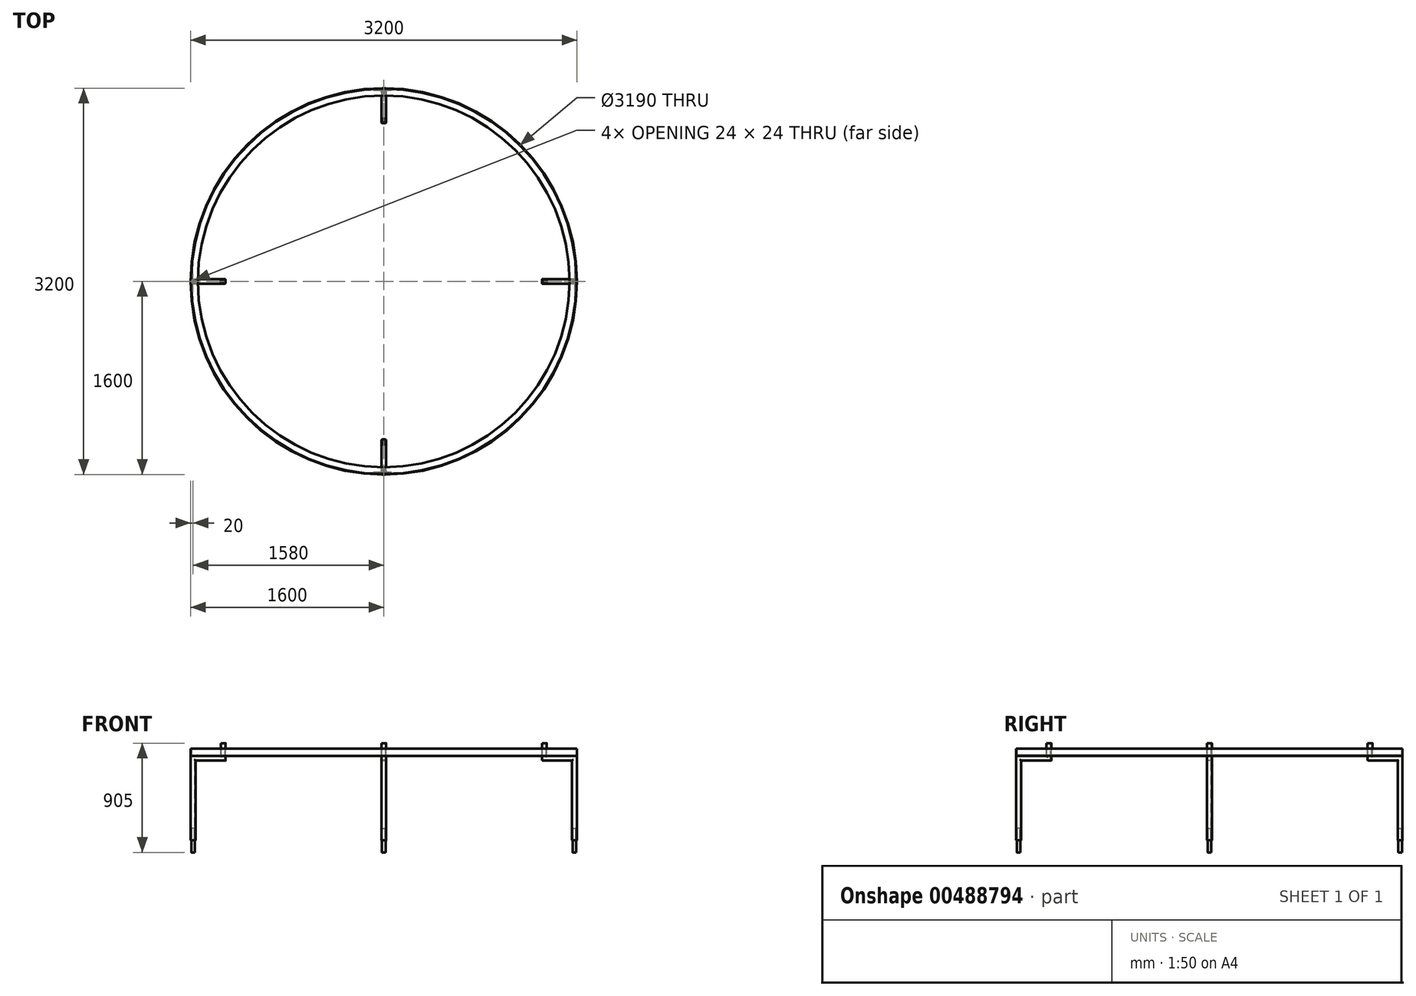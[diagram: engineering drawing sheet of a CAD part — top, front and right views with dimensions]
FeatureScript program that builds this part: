
annotation { "Feature Type Name" : "Feature", "Feature Type Description" : "" }
export const myFeature = defineFeature(function(context is Context, id is Id, definition is map)
    precondition{}
    {
        {
            var Q0;
            Q0=qCreatedBy(makeId("Front.planeOp"),FACE);
            var sketch = newSketch(context, id + "F0", { "sketchPlane" : qUnion([Q0])});
            skLineSegment(sketch, "E0", {"start": v(0, 0) * mm, "end": v(0, 129.65) * mm, "construction": true});
            skLineSegment(sketch, "E1", {"start": v(1540, 0) * mm, "end": v(1600, 0) * mm});
            skLineSegment(sketch, "E2", {"start": v(1600, 0) * mm, "end": v(1600, 60) * mm});
            skLineSegment(sketch, "E3.0", {"start": v(1595, 10) * mm, "end": v(1595, 55) * mm});
            skLineSegment(sketch, "E3.1", {"start": v(1545, 5) * mm, "end": v(1590, 5) * mm});
            skLineSegment(sketch, "E4", {"start": v(1600, 60) * mm, "end": v(1600, 60) * mm});
            skLineSegment(sketch, "E5", {"start": v(1540, 0) * mm, "end": v(1540, 0) * mm});
            skPoint(sketch, "E6.visualSharp", {"position": v(1595, 5) * mm});
            skArc(sketch, "E6.filletArc", {"start": v(1590, 5) * mm, "mid": v(1593.54, 6.46) * mm, "end": v(1595, 10) * mm});
            skPoint(sketch, "E7.visualSharp", {"position": v(1595, 60) * mm});
            skArc(sketch, "E7.filletArc", {"start": v(1600, 60) * mm, "mid": v(1596.46, 58.54) * mm, "end": v(1595, 55) * mm});
            skPoint(sketch, "E8.visualSharp", {"position": v(1540, 5) * mm});
            skArc(sketch, "E8.filletArc", {"start": v(1545, 5) * mm, "mid": v(1541.46, 3.54) * mm, "end": v(1540, 0) * mm});
            skSolve(sketch);
        }
        {
            var Q0;
            Q0=makeQuery(id+"F0.imprint","IMPRINT",FACE,{"disambiguationData":[TD([[makeQuery(id+"F0.imprint","IMPRINT",EDGE,{"derivedFrom":sQuery(id+"F0.wireOp",EDGE,"E1")}),1.0]])]});
            var Q1;
            Q1=sQuery(id+"F0.wireOp",EDGE,"E0");
            revolve(context, id + "F1", {"entities" : qUnion([Q0]), "axis" : qUnion([Q1]), "revolveType" : RevolveType.FULL});
        }
        {
            var Q0;
            Q0=qCreatedBy(makeId("Right.planeOp"),FACE);
            var sketch = newSketch(context, id + "F2", { "sketchPlane" : qUnion([Q0])});
            skLineSegment(sketch, "E9", {"start": v(-1755, -270) * mm, "end": v(-1580, -270) * mm});
            skLineSegment(sketch, "E10", {"start": v(-1580, -270) * mm, "end": v(-1580, -20) * mm});
            skLineSegment(sketch, "E11", {"start": v(-1580, -20) * mm, "end": v(-1330, -20) * mm});
            skLineSegment(sketch, "E12", {"start": v(-1330, -20) * mm, "end": v(-1330, 105) * mm});
            skSolve(sketch);
        }
        {
            var Q0;
            Q0=qCreatedBy(makeId("Front.planeOp"),FACE);
            var Q1;
            Q1=sQuery(id+"F2.wireOp",VERTEX,"E9.start");
            cPlane(context, id + "F3", {"entities" : qUnion([Q0, Q1]), "cplaneType" : CPlaneType.PLANE_POINT, "offset" : 25 * mm, "width" : 150 * mm, "height" : 150 * mm});
        }
        {
            var Q0;
            Q0=qCreatedBy(id+"F3.planeOp",FACE);
            var sketch = newSketch(context, id + "F4", { "sketchPlane" : qUnion([Q0])});
            skLineSegment(sketch, "E13.bottom", {"start": v(12, -290) * mm, "end": v(-12, -290) * mm});
            skLineSegment(sketch, "E13.top", {"start": v(12, -250) * mm, "end": v(-12, -250) * mm});
            skLineSegment(sketch, "E13.left", {"start": v(20, -282) * mm, "end": v(20, -258) * mm});
            skLineSegment(sketch, "E13.right", {"start": v(-20, -282) * mm, "end": v(-20, -258) * mm});
            skPoint(sketch, "E13.middle", {"position": v(0, -270) * mm});
            skPoint(sketch, "E14.visualSharp", {"position": v(-20, -250) * mm});
            skArc(sketch, "E14.filletArc", {"start": v(-12, -250) * mm, "mid": v(-17.66, -252.34) * mm, "end": v(-20, -258) * mm});
            skPoint(sketch, "E15.visualSharp", {"position": v(20, -250) * mm});
            skArc(sketch, "E15.filletArc", {"start": v(20, -258) * mm, "mid": v(17.66, -252.34) * mm, "end": v(12, -250) * mm});
            skPoint(sketch, "E16.visualSharp", {"position": v(20, -290) * mm});
            skArc(sketch, "E16.filletArc", {"start": v(12, -290) * mm, "mid": v(17.66, -287.66) * mm, "end": v(20, -282) * mm});
            skPoint(sketch, "E17.visualSharp", {"position": v(-20, -290) * mm});
            skArc(sketch, "E17.filletArc", {"start": v(-20, -282) * mm, "mid": v(-17.66, -287.66) * mm, "end": v(-12, -290) * mm});
            skArc(sketch, "E18.0", {"start": v(16, -258) * mm, "mid": v(14.83, -255.17) * mm, "end": v(12, -254) * mm});
            skLineSegment(sketch, "E18.1", {"start": v(16, -282) * mm, "end": v(16, -258) * mm});
            skLineSegment(sketch, "E18.2", {"start": v(12, -254) * mm, "end": v(-12, -254) * mm});
            skArc(sketch, "E18.3", {"start": v(12, -286) * mm, "mid": v(14.83, -284.83) * mm, "end": v(16, -282) * mm});
            skArc(sketch, "E18.4", {"start": v(-12, -254) * mm, "mid": v(-14.83, -255.17) * mm, "end": v(-16, -258) * mm});
            skLineSegment(sketch, "E18.5", {"start": v(-16, -282) * mm, "end": v(-16, -258) * mm});
            skArc(sketch, "E18.6", {"start": v(-16, -282) * mm, "mid": v(-14.83, -284.83) * mm, "end": v(-12, -286) * mm});
            skLineSegment(sketch, "E18.7", {"start": v(12, -286) * mm, "end": v(-12, -286) * mm});
            skSolve(sketch);
        }
        {
            var Q0;
            Q0=makeQuery(id+"F4.imprint","IMPRINT",FACE,{"disambiguationData":[TD([[makeQuery(id+"F4.imprint","IMPRINT",EDGE,{"derivedFrom":sQuery(id+"F4.wireOp",EDGE,"E13.bottom")}),-1.0]])]});
            var Q1;
            Q1=sQuery(id+"F2.wireOp",EDGE,"E9");
            var Q2;
            Q2=sQuery(id+"F2.wireOp",EDGE,"E10");
            var Q3;
            Q3=sQuery(id+"F2.wireOp",EDGE,"E11");
            var Q4;
            Q4=sQuery(id+"F2.wireOp",EDGE,"E12");
            sweep(context, id + "F5", {"profiles" : qUnion([Q0]), "path" : qUnion([Q1, Q2, Q3, Q4])});
        }
        {
            var Q0;
            Q0=makeQuery(id+"F5.opSweep","SWEPT_FACE",FACE,{"disambiguationData":[OSD([sQuery(id+"F2.wireOp",EDGE,"E9"),sQuery(id+"F4.wireOp",EDGE,"E13.right")])]});
            var sketch = newSketch(context, id + "F6", { "sketchPlane" : qUnion([Q0])});
            skLineSegment(sketch, "E19.bottom", {"start": v(1755, -250) * mm, "end": v(1560, -250) * mm});
            skLineSegment(sketch, "E19.top", {"start": v(1755, -290) * mm, "end": v(1560, -290) * mm});
            skLineSegment(sketch, "E19.left", {"start": v(1755, -250) * mm, "end": v(1755, -290) * mm});
            skLineSegment(sketch, "E19.right", {"start": v(1560, -250) * mm, "end": v(1560, -290) * mm});
            skSolve(sketch);
        }
        {
            var Q0;
            Q0 = qSketchRegion(id + "F6", true);
            extrude(context, id + "F7", {"entities" : qUnion([Q0]), "operationType" : NewBodyOperationType.REMOVE, "endBound" : BoundingType.THROUGH_ALL, "oppositeDirection" : true, "depth" : 25 * mm});
        }
        {
            var Q0;
            Q0=makeQuery(id+"F7.boolean.opBoolean","COPY",FACE,{"derivedFrom":makeQuery(id+"F7.opExtrude","SWEPT_FACE",FACE,{"disambiguationData":[OSD([sQuery(id+"F6.wireOp",EDGE,"E19.bottom")])]})});
            var sketch = newSketch(context, id + "F8", { "sketchPlane" : qUnion([Q0])});
            skArc(sketch, "E20.0", {"start": v(20, 1592) * mm, "mid": v(17.66, 1597.66) * mm, "end": v(12, 1600) * mm});
            skLineSegment(sketch, "E20.1", {"start": v(20, 1568) * mm, "end": v(20, 1592) * mm});
            skLineSegment(sketch, "E20.2", {"start": v(12, 1600) * mm, "end": v(-12, 1600) * mm});
            skArc(sketch, "E20.3", {"start": v(12, 1560) * mm, "mid": v(17.66, 1562.34) * mm, "end": v(20, 1568) * mm});
            skLineSegment(sketch, "E20.4", {"start": v(12, 1560) * mm, "end": v(-12, 1560) * mm});
            skArc(sketch, "E20.5", {"start": v(-20, 1568) * mm, "mid": v(-17.66, 1562.34) * mm, "end": v(-12, 1560) * mm});
            skLineSegment(sketch, "E20.6", {"start": v(-20, 1592) * mm, "end": v(-20, 1568) * mm});
            skArc(sketch, "E20.7", {"start": v(-12, 1600) * mm, "mid": v(-17.66, 1597.66) * mm, "end": v(-20, 1592) * mm});
            skLineSegment(sketch, "E20.8", {"start": v(-12, 1596) * mm, "end": v(12, 1596) * mm});
            skArc(sketch, "E20.9", {"start": v(12, 1596) * mm, "mid": v(14.83, 1594.83) * mm, "end": v(16, 1592) * mm});
            skLineSegment(sketch, "E20.10", {"start": v(16, 1592) * mm, "end": v(16, 1568) * mm});
            skArc(sketch, "E20.11", {"start": v(16, 1568) * mm, "mid": v(14.83, 1565.17) * mm, "end": v(12, 1564) * mm});
            skLineSegment(sketch, "E20.12", {"start": v(12, 1564) * mm, "end": v(-12, 1564) * mm});
            skArc(sketch, "E20.13", {"start": v(-12, 1564) * mm, "mid": v(-14.83, 1565.17) * mm, "end": v(-16, 1568) * mm});
            skLineSegment(sketch, "E20.14", {"start": v(-16, 1568) * mm, "end": v(-16, 1592) * mm});
            skArc(sketch, "E20.15", {"start": v(-16, 1592) * mm, "mid": v(-14.83, 1594.83) * mm, "end": v(-12, 1596) * mm});
            skSolve(sketch);
        }
        {
            var Q0;
            Q0 = qSketchRegion(id + "F8", true);
            extrude(context, id + "F9", {"entities" : qUnion([Q0]), "operationType" : NewBodyOperationType.ADD, "depth" : 450 * mm});
        }
        {
            var Q0;
            Q0=makeQuery(id+"F9.opExtrude","CAP_FACE",FACE,{"disambiguationData":[OSD([sQuery(id+"F8.wireOp",EDGE,"E20.0"),sQuery(id+"F8.wireOp",EDGE,"E20.1"),sQuery(id+"F8.wireOp",EDGE,"E20.2"),sQuery(id+"F8.wireOp",EDGE,"E20.3"),sQuery(id+"F8.wireOp",EDGE,"E20.4"),sQuery(id+"F8.wireOp",EDGE,"E20.5"),sQuery(id+"F8.wireOp",EDGE,"E20.6"),sQuery(id+"F8.wireOp",EDGE,"E20.7"),sQuery(id+"F8.wireOp",EDGE,"E20.8"),sQuery(id+"F8.wireOp",EDGE,"E20.9"),sQuery(id+"F8.wireOp",EDGE,"E20.10"),sQuery(id+"F8.wireOp",EDGE,"E20.11"),sQuery(id+"F8.wireOp",EDGE,"E20.12"),sQuery(id+"F8.wireOp",EDGE,"E20.13"),sQuery(id+"F8.wireOp",EDGE,"E20.14"),sQuery(id+"F8.wireOp",EDGE,"E20.15")])],"isStart":false});
            var sketch = newSketch(context, id + "F10", { "sketchPlane" : qUnion([Q0])});
            skLineSegment(sketch, "E21.bottom", {"start": v(9, 1565) * mm, "end": v(-9, 1565) * mm});
            skLineSegment(sketch, "E21.top", {"start": v(9, 1595) * mm, "end": v(-9, 1595) * mm});
            skLineSegment(sketch, "E21.left", {"start": v(15, 1571) * mm, "end": v(15, 1589) * mm});
            skLineSegment(sketch, "E21.right", {"start": v(-15, 1571) * mm, "end": v(-15, 1589) * mm});
            skPoint(sketch, "E21.middle", {"position": v(0, 1580) * mm});
            skPoint(sketch, "E21.middle.positionSnap0", {"position": v(-20, 1580) * mm});
            skPoint(sketch, "E21.middle.positionSnap1", {"position": v(0, 1596) * mm});
            skPoint(sketch, "E21.centerSnap0", {"position": v(-20, 1580) * mm});
            skPoint(sketch, "E21.centerSnap1", {"position": v(0, 1596) * mm});
            skPoint(sketch, "E22.visualSharp", {"position": v(-15, 1595) * mm});
            skArc(sketch, "E22.filletArc", {"start": v(-9, 1595) * mm, "mid": v(-13.24, 1593.24) * mm, "end": v(-15, 1589) * mm});
            skPoint(sketch, "E23.visualSharp", {"position": v(15, 1595) * mm});
            skArc(sketch, "E23.filletArc", {"start": v(15, 1589) * mm, "mid": v(13.24, 1593.24) * mm, "end": v(9, 1595) * mm});
            skPoint(sketch, "E24.visualSharp", {"position": v(15, 1565) * mm});
            skArc(sketch, "E24.filletArc", {"start": v(9, 1565) * mm, "mid": v(13.24, 1566.76) * mm, "end": v(15, 1571) * mm});
            skPoint(sketch, "E25.visualSharp", {"position": v(-15, 1565) * mm});
            skArc(sketch, "E25.filletArc", {"start": v(-15, 1571) * mm, "mid": v(-13.24, 1566.76) * mm, "end": v(-9, 1565) * mm});
            skArc(sketch, "E26.0", {"start": v(9, 1568) * mm, "mid": v(11.12, 1568.88) * mm, "end": v(12, 1571) * mm});
            skLineSegment(sketch, "E26.1", {"start": v(9, 1568) * mm, "end": v(-9, 1568) * mm});
            skLineSegment(sketch, "E26.2", {"start": v(12, 1571) * mm, "end": v(12, 1589) * mm});
            skArc(sketch, "E26.3", {"start": v(-12, 1571) * mm, "mid": v(-11.12, 1568.88) * mm, "end": v(-9, 1568) * mm});
            skArc(sketch, "E26.4", {"start": v(12, 1589) * mm, "mid": v(11.12, 1591.12) * mm, "end": v(9, 1592) * mm});
            skLineSegment(sketch, "E26.5", {"start": v(9, 1592) * mm, "end": v(-9, 1592) * mm});
            skArc(sketch, "E26.6", {"start": v(-9, 1592) * mm, "mid": v(-11.12, 1591.12) * mm, "end": v(-12, 1589) * mm});
            skLineSegment(sketch, "E26.7", {"start": v(-12, 1571) * mm, "end": v(-12, 1589) * mm});
            skSolve(sketch);
        }
        {
            var Q0;
            Q0 = qSketchRegion(id + "F10", true);
            extrude(context, id + "F11", {"entities" : qUnion([Q0]), "depth" : 100 * mm, "hasSecondDirection" : true, "secondDirectionOppositeDirection" : true, "secondDirectionDepth" : 100 * mm});
        }
        {
            var Q0;
            Q0=makeQuery(id+"F5.opSweep","SWEPT_BODY",BODY,{"disambiguationData":[OSD([sQuery(id+"F2.wireOp",EDGE,"E12"),sQuery(id+"F4.wireOp",EDGE,"E13.bottom"),sQuery(id+"F4.wireOp",EDGE,"E13.top"),sQuery(id+"F4.wireOp",EDGE,"E13.left"),sQuery(id+"F4.wireOp",EDGE,"E13.right"),sQuery(id+"F4.wireOp",EDGE,"E14.filletArc"),sQuery(id+"F4.wireOp",EDGE,"E15.filletArc"),sQuery(id+"F4.wireOp",EDGE,"E16.filletArc"),sQuery(id+"F4.wireOp",EDGE,"E17.filletArc"),sQuery(id+"F4.wireOp",EDGE,"E18.0"),sQuery(id+"F4.wireOp",EDGE,"E18.1"),sQuery(id+"F4.wireOp",EDGE,"E18.2"),sQuery(id+"F4.wireOp",EDGE,"E18.3"),sQuery(id+"F4.wireOp",EDGE,"E18.4"),sQuery(id+"F4.wireOp",EDGE,"E18.5"),sQuery(id+"F4.wireOp",EDGE,"E18.6"),sQuery(id+"F4.wireOp",EDGE,"E18.7")])]});
            var Q1;
            Q1=makeQuery(id+"F11.opExtrude","SWEPT_BODY",BODY,{"disambiguationData":[OSD([sQuery(id+"F10.wireOp",EDGE,"E21.bottom"),sQuery(id+"F10.wireOp",EDGE,"E21.top"),sQuery(id+"F10.wireOp",EDGE,"E21.left"),sQuery(id+"F10.wireOp",EDGE,"E21.right"),sQuery(id+"F10.wireOp",EDGE,"E22.filletArc"),sQuery(id+"F10.wireOp",EDGE,"E23.filletArc"),sQuery(id+"F10.wireOp",EDGE,"E24.filletArc"),sQuery(id+"F10.wireOp",EDGE,"E25.filletArc"),sQuery(id+"F10.wireOp",EDGE,"E26.0"),sQuery(id+"F10.wireOp",EDGE,"E26.1"),sQuery(id+"F10.wireOp",EDGE,"E26.2"),sQuery(id+"F10.wireOp",EDGE,"E26.3"),sQuery(id+"F10.wireOp",EDGE,"E26.4"),sQuery(id+"F10.wireOp",EDGE,"E26.5"),sQuery(id+"F10.wireOp",EDGE,"E26.6"),sQuery(id+"F10.wireOp",EDGE,"E26.7")])]});
            var Q2;
            Q2=makeQuery(id+"F1.opRevolve","SWEPT_EDGE",EDGE,{"disambiguationData":[OSD([sQuery(id+"F0.wireOp",EDGE,"E2"),sQuery(id+"F0.wireOp",EDGE,"E7.filletArc")])]});
            circularPattern(context, id + "F12", {"entities" : qUnion([Q0, Q1]), "axis" : qUnion([Q2]), "angle" : 360 * degree, "instanceCount" : 4, "equalSpace" : true});
        }
    });
